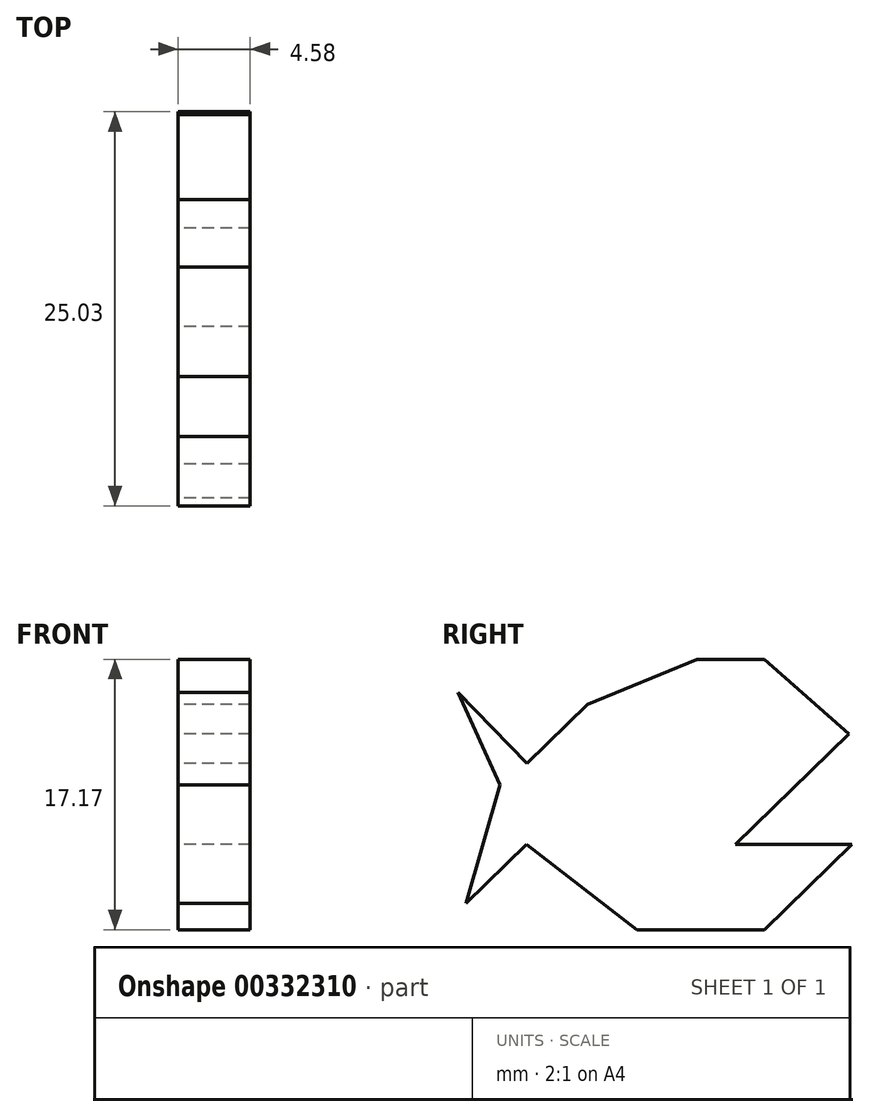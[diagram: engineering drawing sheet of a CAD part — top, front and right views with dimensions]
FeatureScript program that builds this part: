
annotation { "Feature Type Name" : "Feature", "Feature Type Description" : "" }
export const myFeature = defineFeature(function(context is Context, id is Id, definition is map)
    precondition{}
    {
        {
            var Q0;
            Q0=qCreatedBy(makeId("Right.planeOp"),FACE);
            var sketch = newSketch(context, id + "F0", { "sketchPlane" : qUnion([Q0])});
            skLineSegment(sketch, "E0", {"start": v(51.2, 32.04) * mm, "end": v(43.99, 25.03) * mm});
            skLineSegment(sketch, "E1", {"start": v(43.99, 25.03) * mm, "end": v(51.38, 25.03) * mm});
            skLineSegment(sketch, "E2", {"start": v(51.38, 25.03) * mm, "end": v(45.81, 19.6) * mm});
            skLineSegment(sketch, "E3", {"start": v(45.81, 19.6) * mm, "end": v(37.73, 19.6) * mm});
            skLineSegment(sketch, "E4", {"start": v(37.73, 19.6) * mm, "end": v(30.71, 25.03) * mm});
            skLineSegment(sketch, "E5", {"start": v(30.71, 25.03) * mm, "end": v(26.86, 21.28) * mm});
            skLineSegment(sketch, "E6", {"start": v(26.86, 21.28) * mm, "end": v(29, 28.82) * mm});
            skLineSegment(sketch, "E7", {"start": v(29, 28.82) * mm, "end": v(26.35, 34.7) * mm});
            skLineSegment(sketch, "E8", {"start": v(26.35, 34.7) * mm, "end": v(30.75, 30.19) * mm});
            skLineSegment(sketch, "E9", {"start": v(30.75, 30.19) * mm, "end": v(34.56, 33.9) * mm});
            skLineSegment(sketch, "E10", {"start": v(34.56, 33.9) * mm, "end": v(41.52, 36.78) * mm});
            skLineSegment(sketch, "E11", {"start": v(41.52, 36.78) * mm, "end": v(45.81, 36.78) * mm});
            skLineSegment(sketch, "E12", {"start": v(45.81, 36.78) * mm, "end": v(51.2, 32.04) * mm});
            skLineSegment(sketch, "E13", {"start": v(48.5, 34.41) * mm, "end": v(54.52, 41.24) * mm});
            skLineSegment(sketch, "E14", {"start": v(54.52, 41.24) * mm, "end": v(61.62, 29.39) * mm});
            skPoint(sketch, "E15", {"position": v(61.62, 29.39) * mm});
            skSolve(sketch);
        }
        {
            var Q0;
            {var subQ0=sQuery(id+"F0.wireOp",EDGE,"E0");Q0=makeQuery(id+"F0.imprint","IMPRINT",FACE,{"disambiguationData":[TD([[makeQuery(id+"F0.imprint","IMPRINT",EDGE,{"derivedFrom":subQ0}),-1.0]])]});}
            extrude(context, id + "F1", {"entities" : qUnion([Q0]), "endBound" : BoundingType.SYMMETRIC, "depth" : 4.57 * mm});
        }
    });
